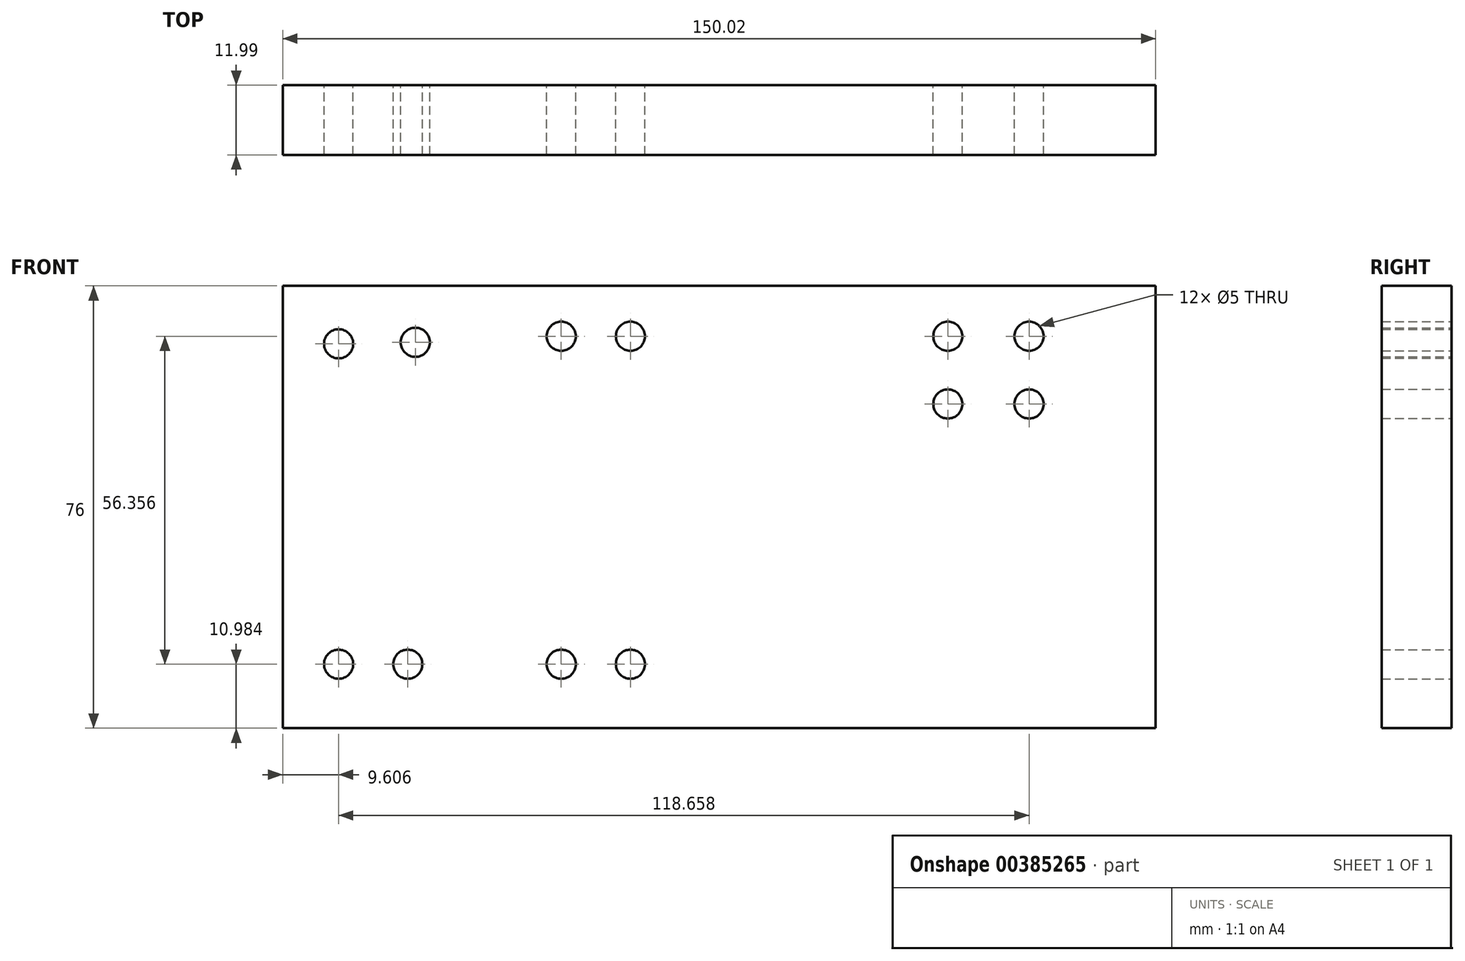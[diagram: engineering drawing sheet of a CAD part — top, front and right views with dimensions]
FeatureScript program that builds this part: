
annotation { "Feature Type Name" : "Feature", "Feature Type Description" : "" }
export const myFeature = defineFeature(function(context is Context, id is Id, definition is map)
    precondition{}
    {
        {
            var Q0;
            Q0=qCreatedBy(makeId("Front.planeOp"),FACE);
            var sketch = newSketch(context, id + "F0", { "sketchPlane" : qUnion([Q0])});
            skLineSegment(sketch, "E0.bottom", {"start": v(-75, 38) * mm, "end": v(75, 38) * mm});
            skLineSegment(sketch, "E0.top", {"start": v(-75, -38) * mm, "end": v(75, -38) * mm});
            skLineSegment(sketch, "E0.left", {"start": v(-75, 38) * mm, "end": v(-75, -38) * mm});
            skLineSegment(sketch, "E0.right", {"start": v(75, 38) * mm, "end": v(75, -38) * mm});
            skPoint(sketch, "E0.middle", {"position": v(0, 0) * mm});
            skCircle(sketch, "E1", {"center": v(-65.4, 28.05) * mm, "radius": 2.5 * mm});
            skCircle(sketch, "E2", {"center": v(-52.22, 28.3) * mm, "radius": 2.5 * mm});
            skCircle(sketch, "E3", {"center": v(-65.4, -27.02) * mm, "radius": 2.5 * mm});
            skCircle(sketch, "E4", {"center": v(-53.51, -27.02) * mm, "radius": 2.5 * mm});
            skCircle(sketch, "E5", {"center": v(-27.14, 29.34) * mm, "radius": 2.5 * mm});
            skCircle(sketch, "E6", {"center": v(-15.25, 29.34) * mm, "radius": 2.5 * mm});
            skCircle(sketch, "E7", {"center": v(-27.14, -27.02) * mm, "radius": 2.5 * mm});
            skCircle(sketch, "E8", {"center": v(-15.25, -27.02) * mm, "radius": 2.5 * mm});
            skCircle(sketch, "E9", {"center": v(39.3, 29.34) * mm, "radius": 2.5 * mm});
            skCircle(sketch, "E10", {"center": v(53.25, 29.34) * mm, "radius": 2.5 * mm});
            skCircle(sketch, "E11", {"center": v(39.3, 17.7) * mm, "radius": 2.5 * mm});
            skCircle(sketch, "E12", {"center": v(53.25, 17.7) * mm, "radius": 2.5 * mm});
            skSolve(sketch);
        }
        {
            var Q0;
            Q0=makeQuery(id+"F0.imprint","IMPRINT",FACE,{"disambiguationData":[TD([[makeQuery(id+"F0.imprint","IMPRINT",EDGE,{"derivedFrom":sQuery(id+"F0.wireOp",EDGE,"E0.bottom")}),-1.0]])]});
            extrude(context, id + "F1", {"entities" : qUnion([Q0]), "depth" : 12 * mm});
        }
    });
